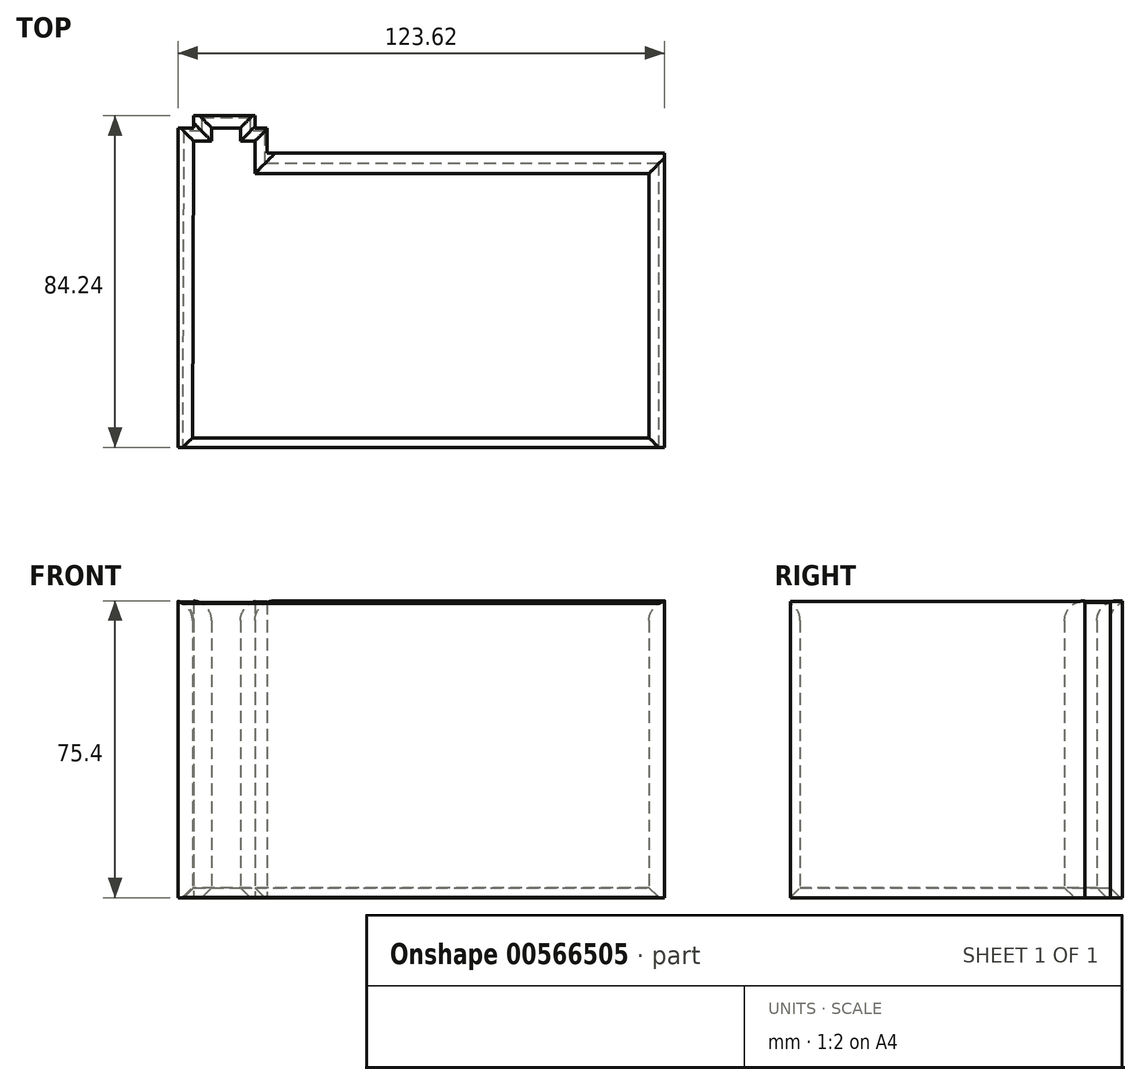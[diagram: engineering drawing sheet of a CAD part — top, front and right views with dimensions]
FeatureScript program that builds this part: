
annotation { "Feature Type Name" : "Feature", "Feature Type Description" : "" }
export const myFeature = defineFeature(function(context is Context, id is Id, definition is map)
    precondition{}
    {
        {
            var Q0;
            Q0=qCreatedBy(makeId("Top.planeOp"),FACE);
            var sketch = newSketch(context, id + "F0", { "sketchPlane" : qUnion([Q0])});
            skLineSegment(sketch, "E0", {"start": v(55.55, 37.87) * mm, "end": v(55.55, -34.47) * mm});
            skLineSegment(sketch, "E1", {"start": v(55.55, -36.91) * mm, "end": v(-68.07, -36.91) * mm});
            skLineSegment(sketch, "E2", {"start": v(-68.07, -36.91) * mm, "end": v(-68.07, 37.87) * mm});
            skLineSegment(sketch, "E3", {"start": v(55.55, -34.47) * mm, "end": v(55.55, -36.91) * mm});
            skLineSegment(sketch, "E4", {"start": v(51.58, 32.68) * mm, "end": v(51.58, -34.47) * mm});
            skLineSegment(sketch, "E5", {"start": v(51.58, -34.47) * mm, "end": v(-64.41, -34.47) * mm});
            skLineSegment(sketch, "E6", {"start": v(55.55, 37.87) * mm, "end": v(-45.5, 37.87) * mm});
            skLineSegment(sketch, "E7", {"start": v(51.58, 32.68) * mm, "end": v(-48.54, 32.68) * mm});
            skLineSegment(sketch, "E8", {"start": v(-45.5, 37.87) * mm, "end": v(-45.5, 44.28) * mm});
            skLineSegment(sketch, "E9", {"start": v(-45.5, 44.28) * mm, "end": v(-48.54, 44.28) * mm});
            skLineSegment(sketch, "E10", {"start": v(-48.54, 44.28) * mm, "end": v(-48.54, 47.33) * mm});
            skLineSegment(sketch, "E11", {"start": v(-48.54, 47.33) * mm, "end": v(-64.1, 47.33) * mm});
            skLineSegment(sketch, "E12", {"start": v(-64.1, 47.33) * mm, "end": v(-64.1, 44.28) * mm});
            skLineSegment(sketch, "E13", {"start": v(-64.1, 44.28) * mm, "end": v(-68.07, 44.28) * mm});
            skLineSegment(sketch, "E14", {"start": v(-68.07, 44.28) * mm, "end": v(-68.07, 32.68) * mm});
            skLineSegment(sketch, "E15", {"start": v(-48.54, 32.68) * mm, "end": v(-48.54, 40.92) * mm});
            skLineSegment(sketch, "E16", {"start": v(-48.54, 40.92) * mm, "end": v(-52.2, 40.92) * mm});
            skLineSegment(sketch, "E17", {"start": v(-52.2, 40.92) * mm, "end": v(-52.2, 44.28) * mm});
            skLineSegment(sketch, "E18", {"start": v(-52.2, 44.28) * mm, "end": v(-59.53, 44.28) * mm});
            skLineSegment(sketch, "E19", {"start": v(-59.53, 44.28) * mm, "end": v(-59.53, 40.92) * mm});
            skLineSegment(sketch, "E20", {"start": v(-59.53, 40.92) * mm, "end": v(-64.1, 40.92) * mm});
            skLineSegment(sketch, "E21", {"start": v(-64.1, 40.92) * mm, "end": v(-64.41, -34.47) * mm});
            skSolve(sketch);
        }
        {
            var Q0;
            Q0=makeQuery(id+"F0.imprint","IMPRINT",FACE,{"disambiguationData":[TD([[makeQuery(id+"F0.imprint","IMPRINT",EDGE,{"derivedFrom":sQuery(id+"F0.wireOp",EDGE,"E0")}),-1.0]])]});
            extrude(context, id + "F1", {"entities" : qUnion([Q0]), "depth" : 50 * mm, "offsetDistance" : 25.4 * mm});
        }
        {
            var Q0;
            Q0 = qSketchRegion(id + "F0", true);
            var Q1;
            Q1=makeQuery(id+"F1.opExtrude","CAP_FACE",FACE,{"disambiguationData":[OSD([sQuery(id+"F0.wireOp",EDGE,"E0"),sQuery(id+"F0.wireOp",EDGE,"E1"),sQuery(id+"F0.wireOp",EDGE,"E2"),sQuery(id+"F0.wireOp",EDGE,"E3"),sQuery(id+"F0.wireOp",EDGE,"E4"),sQuery(id+"F0.wireOp",EDGE,"E5"),sQuery(id+"F0.wireOp",EDGE,"E6"),sQuery(id+"F0.wireOp",EDGE,"E7"),sQuery(id+"F0.wireOp",EDGE,"E8"),sQuery(id+"F0.wireOp",EDGE,"E9"),sQuery(id+"F0.wireOp",EDGE,"E10"),sQuery(id+"F0.wireOp",EDGE,"E11"),sQuery(id+"F0.wireOp",EDGE,"E12"),sQuery(id+"F0.wireOp",EDGE,"E13"),sQuery(id+"F0.wireOp",EDGE,"E14"),sQuery(id+"F0.wireOp",EDGE,"E15"),sQuery(id+"F0.wireOp",EDGE,"E16"),sQuery(id+"F0.wireOp",EDGE,"E17"),sQuery(id+"F0.wireOp",EDGE,"E18"),sQuery(id+"F0.wireOp",EDGE,"E19"),sQuery(id+"F0.wireOp",EDGE,"E20"),sQuery(id+"F0.wireOp",EDGE,"E21")])],"isStart":false});
            extrude(context, id + "F2", {"entities" : qUnion([Q0, Q1]), "operationType" : NewBodyOperationType.ADD, "depth" : 25.4 * mm, "offsetDistance" : 25.4 * mm});
        }
        {
            var Q0;
            {var subQ0=sQuery(id+"F0.wireOp",EDGE,"E21");Q0=makeQuery(id+"F2.opExtrude","CAP_EDGE",EDGE,{"disambiguationData":[OSD([subQ0]),TDD([makeQuery(id+"F1.opExtrude","CAP_EDGE",EDGE,{"disambiguationData":[OSD([subQ0])],"isStart":false})])],"isStart":false});}
            var Q1;
            {var subQ0=sQuery(id+"F0.wireOp",EDGE,"E20");Q1=makeQuery(id+"F2.opExtrude","CAP_EDGE",EDGE,{"disambiguationData":[OSD([subQ0]),TDD([makeQuery(id+"F1.opExtrude","CAP_EDGE",EDGE,{"disambiguationData":[OSD([subQ0])],"isStart":false})])],"isStart":false});}
            var Q2;
            {var subQ0=sQuery(id+"F0.wireOp",EDGE,"E18");Q2=makeQuery(id+"F2.opExtrude","CAP_EDGE",EDGE,{"disambiguationData":[OSD([subQ0]),TDD([makeQuery(id+"F1.opExtrude","CAP_EDGE",EDGE,{"disambiguationData":[OSD([subQ0])],"isStart":false})])],"isStart":false});}
            var Q3;
            {var subQ0=sQuery(id+"F0.wireOp",EDGE,"E19");Q3=makeQuery(id+"F2.opExtrude","CAP_EDGE",EDGE,{"disambiguationData":[OSD([subQ0]),TDD([makeQuery(id+"F1.opExtrude","CAP_EDGE",EDGE,{"disambiguationData":[OSD([subQ0])],"isStart":false})])],"isStart":false});}
            var Q4;
            {var subQ0=sQuery(id+"F0.wireOp",EDGE,"E17");Q4=makeQuery(id+"F2.opExtrude","CAP_EDGE",EDGE,{"disambiguationData":[OSD([subQ0]),TDD([makeQuery(id+"F1.opExtrude","CAP_EDGE",EDGE,{"disambiguationData":[OSD([subQ0])],"isStart":false})])],"isStart":false});}
            var Q5;
            {var subQ0=sQuery(id+"F0.wireOp",EDGE,"E15");Q5=makeQuery(id+"F2.opExtrude","CAP_EDGE",EDGE,{"disambiguationData":[OSD([subQ0]),TDD([makeQuery(id+"F1.opExtrude","CAP_EDGE",EDGE,{"disambiguationData":[OSD([subQ0])],"isStart":false})])],"isStart":false});}
            var Q6;
            {var subQ0=sQuery(id+"F0.wireOp",EDGE,"E16");Q6=makeQuery(id+"F2.opExtrude","CAP_EDGE",EDGE,{"disambiguationData":[OSD([subQ0]),TDD([makeQuery(id+"F1.opExtrude","CAP_EDGE",EDGE,{"disambiguationData":[OSD([subQ0])],"isStart":false})])],"isStart":false});}
            var Q7;
            {var subQ0=sQuery(id+"F0.wireOp",EDGE,"E7");Q7=makeQuery(id+"F2.opExtrude","CAP_EDGE",EDGE,{"disambiguationData":[OSD([subQ0]),TDD([makeQuery(id+"F1.opExtrude","CAP_EDGE",EDGE,{"disambiguationData":[OSD([subQ0])],"isStart":false})])],"isStart":false});}
            var Q8;
            {var subQ0=sQuery(id+"F0.wireOp",EDGE,"E4");Q8=makeQuery(id+"F2.opExtrude","CAP_EDGE",EDGE,{"disambiguationData":[OSD([subQ0]),TDD([makeQuery(id+"F1.opExtrude","CAP_EDGE",EDGE,{"disambiguationData":[OSD([subQ0])],"isStart":false})])],"isStart":false});}
            var Q9;
            {var subQ0=sQuery(id+"F0.wireOp",EDGE,"E5");Q9=makeQuery(id+"F2.opExtrude","CAP_EDGE",EDGE,{"disambiguationData":[OSD([subQ0]),TDD([makeQuery(id+"F1.opExtrude","CAP_EDGE",EDGE,{"disambiguationData":[OSD([subQ0])],"isStart":false})])],"isStart":false});}
            fillet(context, id + "F3", {"entities" : qUnion([Q0, Q1, Q2, Q3, Q4, Q5, Q6, Q7, Q8, Q9]), "radius" : 5 * mm, "tangentPropagation" : true, "allowEdgeOverflow" : false});
        }
        {
            var Q0;
            Q0=makeQuery(id+"F1.opExtrude","CAP_EDGE",EDGE,{"disambiguationData":[OSD([sQuery(id+"F0.wireOp",EDGE,"E21")])],"isStart":true});
            var Q1;
            Q1=makeQuery(id+"F1.opExtrude","CAP_EDGE",EDGE,{"disambiguationData":[OSD([sQuery(id+"F0.wireOp",EDGE,"E20")])],"isStart":true});
            var Q2;
            Q2=makeQuery(id+"F1.opExtrude","CAP_EDGE",EDGE,{"disambiguationData":[OSD([sQuery(id+"F0.wireOp",EDGE,"E18")])],"isStart":true});
            var Q3;
            Q3=makeQuery(id+"F1.opExtrude","CAP_EDGE",EDGE,{"disambiguationData":[OSD([sQuery(id+"F0.wireOp",EDGE,"E19")])],"isStart":true});
            var Q4;
            Q4=makeQuery(id+"F1.opExtrude","CAP_EDGE",EDGE,{"disambiguationData":[OSD([sQuery(id+"F0.wireOp",EDGE,"E17")])],"isStart":true});
            var Q5;
            Q5=makeQuery(id+"F1.opExtrude","CAP_EDGE",EDGE,{"disambiguationData":[OSD([sQuery(id+"F0.wireOp",EDGE,"E16")])],"isStart":true});
            var Q6;
            Q6=makeQuery(id+"F1.opExtrude","CAP_EDGE",EDGE,{"disambiguationData":[OSD([sQuery(id+"F0.wireOp",EDGE,"E15")])],"isStart":true});
            var Q7;
            Q7=makeQuery(id+"F1.opExtrude","CAP_EDGE",EDGE,{"disambiguationData":[OSD([sQuery(id+"F0.wireOp",EDGE,"E7")])],"isStart":true});
            var Q8;
            Q8=makeQuery(id+"F1.opExtrude","CAP_EDGE",EDGE,{"disambiguationData":[OSD([sQuery(id+"F0.wireOp",EDGE,"E4")])],"isStart":true});
            var Q9;
            Q9=makeQuery(id+"F1.opExtrude","CAP_EDGE",EDGE,{"disambiguationData":[OSD([sQuery(id+"F0.wireOp",EDGE,"E5")])],"isStart":true});
            chamfer(context, id + "F4", {"entities" : qUnion([Q0, Q1, Q2, Q3, Q4, Q5, Q6, Q7, Q8, Q9]), "width" : 2.54 * mm, "tangentPropagation" : true});
        }
    });
